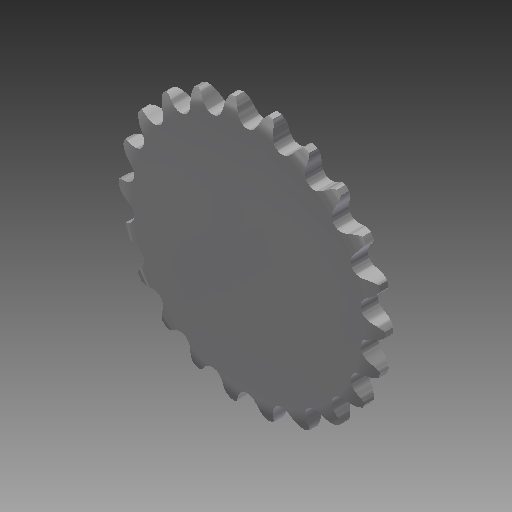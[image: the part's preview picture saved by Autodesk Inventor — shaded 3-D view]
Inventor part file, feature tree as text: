
AUTODESK INVENTOR PART (.ipt)
format: ipt  version: 2017 (Build 210142000, 142)  size: 617,472 bytes
history: native  units: mm
features: other x6, extrude x2, pattern_linear x1, pattern_circular x1
ambient origin geometry x8: Origin, YZ Plane, XZ Plane, XY Plane, X Axis, Y Axis, Z Axis, Center Point
bodies: Solid1 (feature_tree)
feature tree (10):
  other  "Theoretical Tooth Profile"
  other  "Tooth Profile"
  other  "Section Profile"
  other  "Shroud"
  other  "Strand"
  pattern_linear  "Strand Pattern"  Spacing1=44.619381mm  [1 undecoded]
  extrude  "Theoretical Tooth"  Depth=2.855993mm
  extrude  "Tooth"  Depth=1.697355mm
  pattern_circular  "Tooth Pattern"  [2 undecoded]
  other  "Timing Plane"
note: 3 required parameter values undecoded (feature->parameter linkage not recoverable at this tier; creation-order binding heuristic only, values carry confidence <= 0.55)
